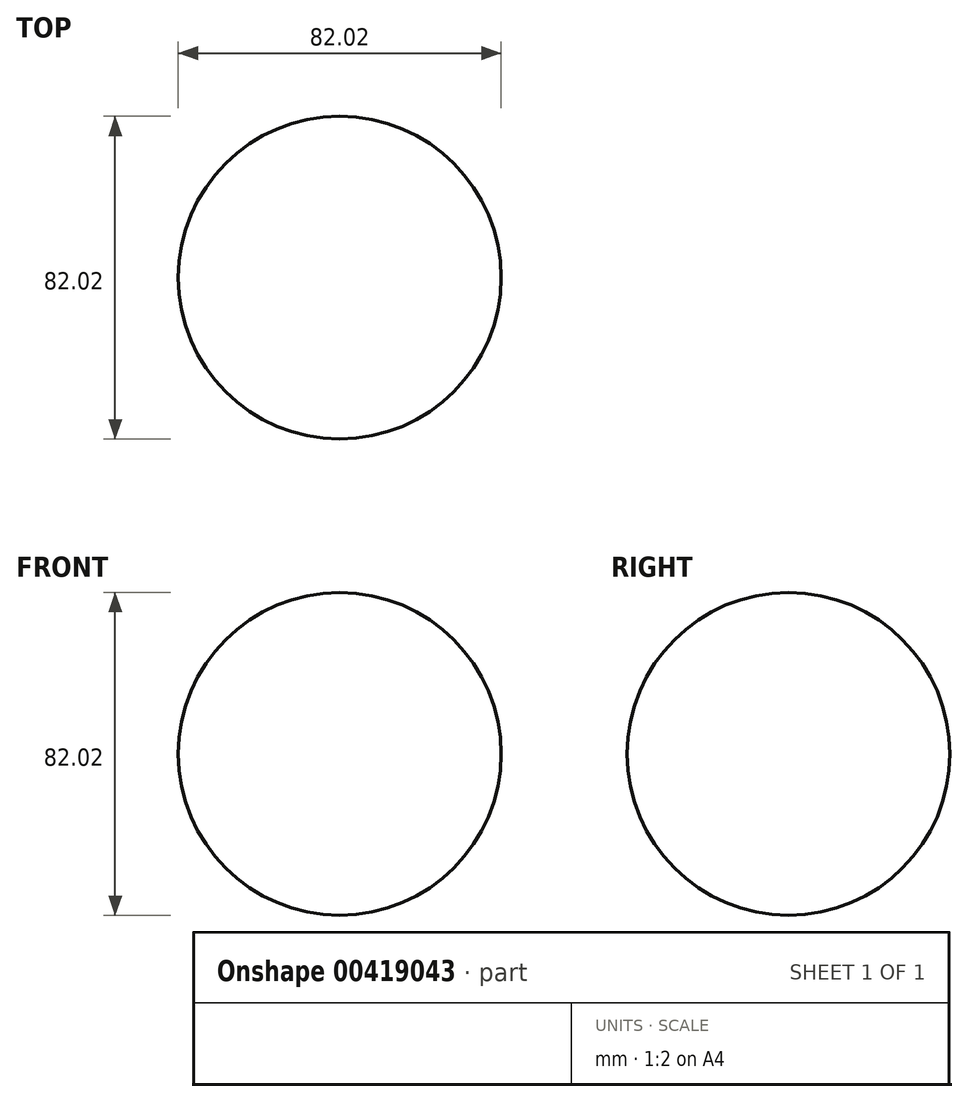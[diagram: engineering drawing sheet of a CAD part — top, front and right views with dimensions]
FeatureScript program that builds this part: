
annotation { "Feature Type Name" : "Feature", "Feature Type Description" : "" }
export const myFeature = defineFeature(function(context is Context, id is Id, definition is map)
    precondition{}
    {
        {
            var Q0;
            Q0=qCreatedBy(makeId("Front.planeOp"),FACE);
            var sketch = newSketch(context, id + "F0", { "sketchPlane" : qUnion([Q0])});
            skArc(sketch, "E0", {"start": v(0, 41) * mm, "mid": v(-41, 0) * mm, "end": v(0, -41) * mm});
            skLineSegment(sketch, "E1", {"start": v(0, 41) * mm, "end": v(0, -41) * mm});
            skSolve(sketch);
        }
        {
            var Q0;
            Q0=makeQuery(id+"F0.imprint","IMPRINT",FACE,{"disambiguationData":[TD([[makeQuery(id+"F0.imprint","IMPRINT",EDGE,{"derivedFrom":sQuery(id+"F0.wireOp",EDGE,"E0")}),1.0]])]});
            var Q1;
            Q1=sQuery(id+"F0.wireOp",EDGE,"E1");
            revolve(context, id + "F1", {"entities" : qUnion([Q0]), "axis" : qUnion([Q1]), "revolveType" : RevolveType.FULL});
        }
    });
